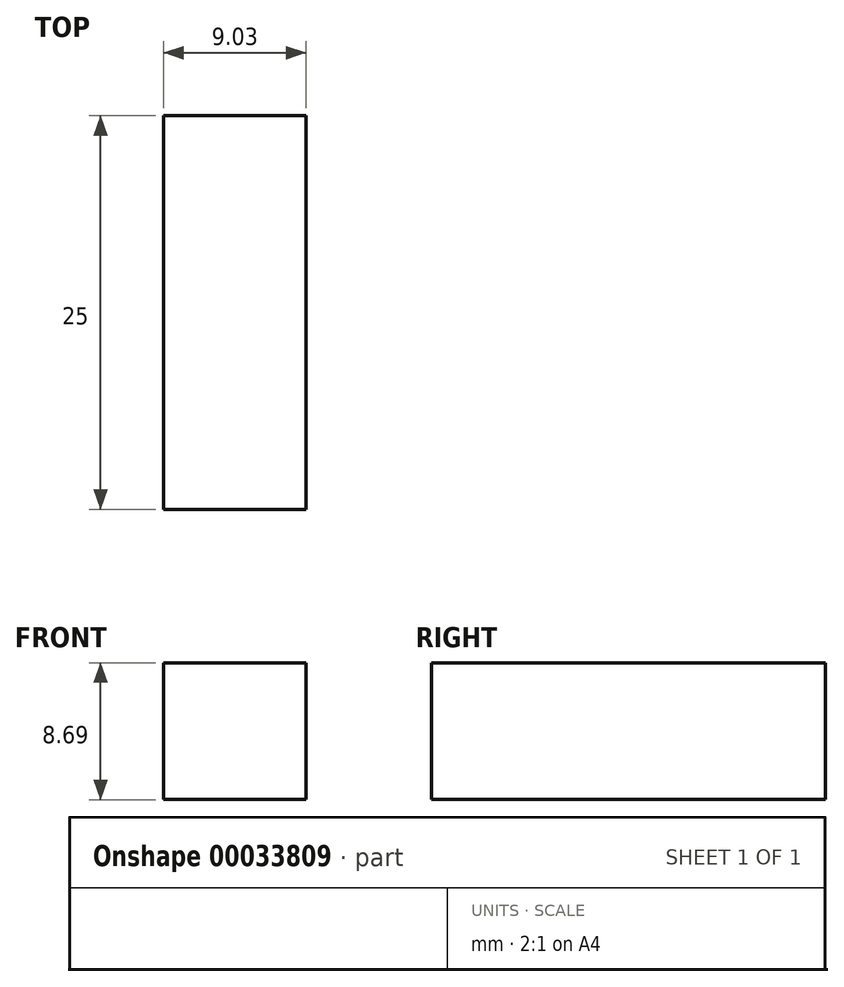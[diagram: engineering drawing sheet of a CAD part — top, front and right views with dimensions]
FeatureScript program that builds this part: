
annotation { "Feature Type Name" : "Feature", "Feature Type Description" : "" }
export const myFeature = defineFeature(function(context is Context, id is Id, definition is map)
    precondition{}
    {
        {
            var Q0;
            Q0=qCreatedBy(makeId("Front.planeOp"),FACE);
            var sketch = newSketch(context, id + "F0", { "sketchPlane" : qUnion([Q0])});
            skLineSegment(sketch, "E0.bottom", {"start": v(-142.63, 55.15) * mm, "end": v(-133.6, 55.15) * mm});
            skLineSegment(sketch, "E0.top", {"start": v(-142.63, 46.46) * mm, "end": v(-133.6, 46.46) * mm});
            skLineSegment(sketch, "E0.left", {"start": v(-142.63, 55.15) * mm, "end": v(-142.63, 46.46) * mm});
            skLineSegment(sketch, "E0.right", {"start": v(-133.6, 55.15) * mm, "end": v(-133.6, 46.46) * mm});
            skSolve(sketch);
        }
        {
            var Q0;
            Q0=makeQuery(id+"F0.imprint","IMPRINT",FACE,{"disambiguationData":[TD([[makeQuery(id+"F0.imprint","IMPRINT",EDGE,{"derivedFrom":sQuery(id+"F0.wireOp",EDGE,"E0.bottom")}),-1.0]])]});
            extrude(context, id + "F1", {"entities" : qUnion([Q0]), "depth" : 25 * mm});
        }
    });
